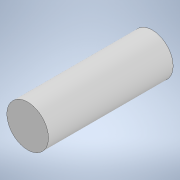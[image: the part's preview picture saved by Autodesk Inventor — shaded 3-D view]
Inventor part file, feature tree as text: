
AUTODESK INVENTOR PART (.ipt)
format: ipt  version: 2022 (Build 260153000, 153)  size: 90,624 bytes
history: native  units: in
note: dims shown in document units (in); Inventor stores cm internally (conversion verified against a paired STEP export)
features: extrude x1, sketch x1
ambient origin geometry x8: Origin, YZ Plane, XZ Plane, XY Plane, X Axis, Y Axis, Z Axis, Center Point
bodies: Solid1 (feature_tree)
feature tree (2):
  extrude  "Extrusion1"  Depth=120.0in TaperAngle=0.0deg
  sketch  "Sketch1"  dims[d0=40.0in d1=120.0in d2=0.0in]
